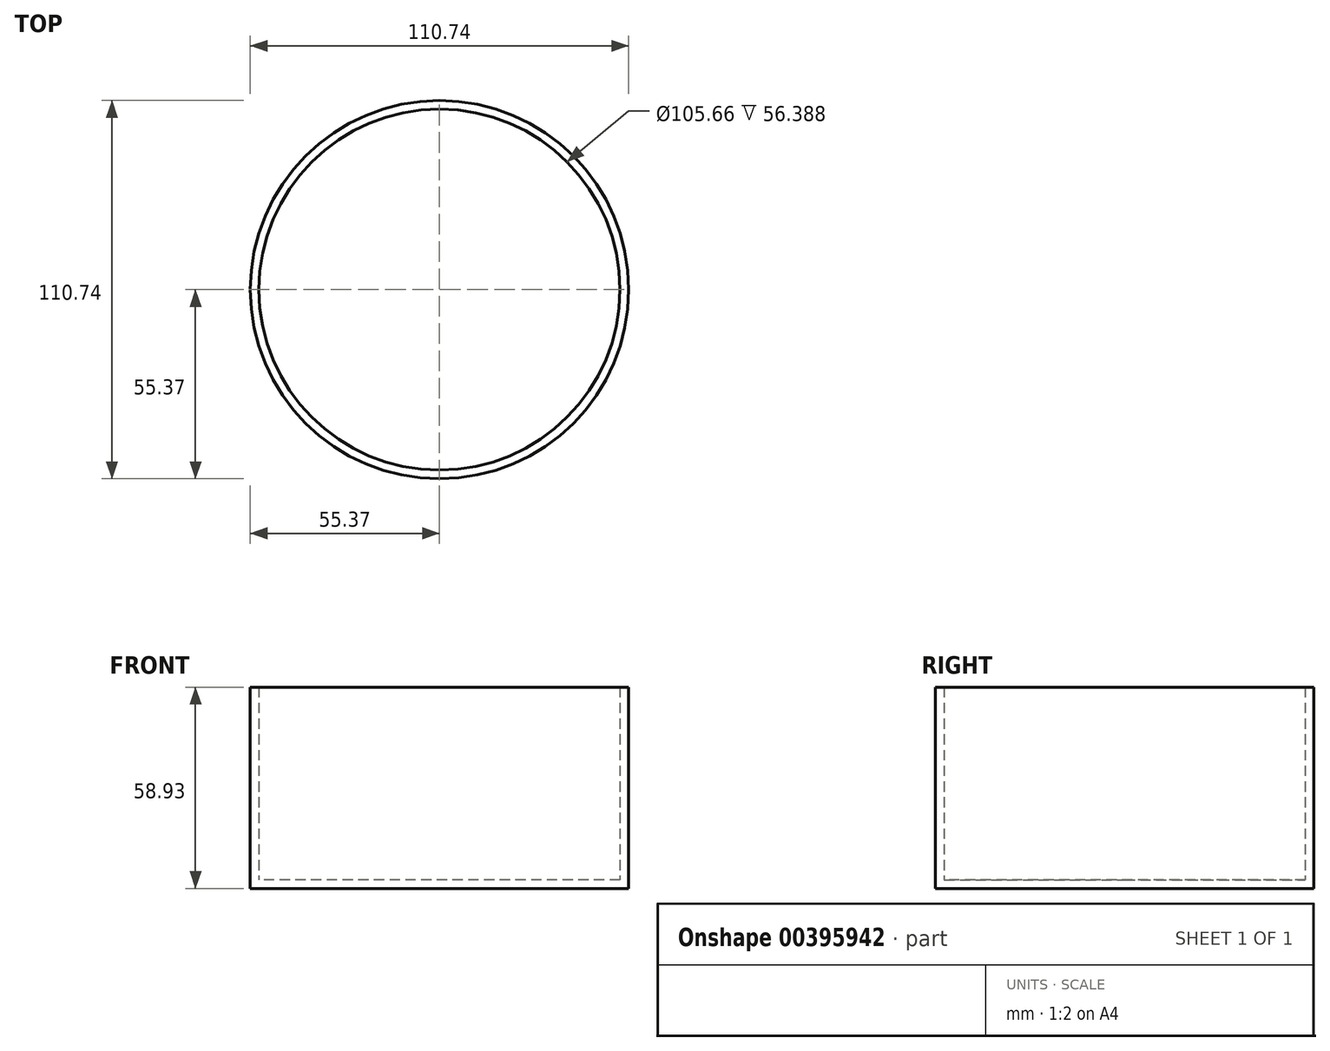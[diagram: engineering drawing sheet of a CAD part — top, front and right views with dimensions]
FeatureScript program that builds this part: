
annotation { "Feature Type Name" : "Feature", "Feature Type Description" : "" }
export const myFeature = defineFeature(function(context is Context, id is Id, definition is map)
    precondition{}
    {
        {
            var Q0;
            Q0=qCreatedBy(makeId("Top.planeOp"),FACE);
            var sketch = newSketch(context, id + "F0", { "sketchPlane" : qUnion([Q0])});
            skCircle(sketch, "E0", {"center": v(0, 0) * mm, "radius": 52.83 * mm});
            skSolve(sketch);
        }
        {
            var Q0;
            Q0=makeQuery(id+"F0.imprint","IMPRINT",FACE,{"disambiguationData":[TD([[makeQuery(id+"F0.imprint","IMPRINT",EDGE,{"derivedFrom":sQuery(id+"F0.wireOp",EDGE,"E0")}),1.0]])]});
            extrude(context, id + "F1", {"entities" : qUnion([Q0]), "depth" : 56.4 * mm});
        }
        {
            var Q0;
            Q0=makeQuery(id+"F1.opExtrude","CAP_FACE",FACE,{"disambiguationData":[OSD([sQuery(id+"F0.wireOp",EDGE,"E0")])],"isStart":false});
            shell(context, id + "F2", {"entities" : qUnion([Q0]), "thickness" : 2.54 * mm, "oppositeDirection" : true});
        }
    });
